# Revit family: Fallrohrstütze DN200-Set
name_source: partatom
category: HLS-Bauteile
revit_build: Autodesk Revit 2017 (Build: 20190507_1515(x64)
units: mm (PartAtom-declared; Revit-internal decimal feet)

## family parameters
Basisbauteil = Fläche
Beim Laden mit Abzugskörper schneiden = Nein
Bemaßung runder Anschluss = Durchmesser verwenden
Gemeinsam genutzt = Ja
Raumberechnungspunkt = Nein
Teiletyp = Normal

## types (1)
- Fallrohrstütze DN200
    6kt.Flanschmutter = Sechskantmutter : Sechskantmutter M12
    6kt.Schraube = 6kt.Schraube DIN EN ISO 4017 : M12x 30 SW19
    Abstandsmaß = 280 mm
    Abstandswinkeltyp = MEFA Winkel 2-Loch C-Profil 45
    Artikelnummer = 45020045
    B = 268 mm  [stored 0.879265 ft]
    Baustoffklasse = B2
    EAN = 4250928448415
    Fabrikat = MEFA
    Farbe Schalldämmeinlage = Schwarz
    Firma = MEFA Befestigungs- und Montagesysteme GmbH
    Gewicht = 4.08 kg
    Gewicht pro Bauteil = 4.08 kg
    Gewindeplattentyp = MEFA Zahnplatte S 36x20 M12
    Konsole = Konsole 45-45 : Konsole 45/45/2,  L=315mm
    Konsolentyp = C-Profil 45/45
    Kurztext1 = Fallrohrstützenbefestigung Set SML
    Kurztext2 = DN 200 / 210 mm Wandabstand 125 - 315 mm
    Langloch = 20 x 14 mm
    Lochabstand = 85 mm
    Länge Konsole = 315 mm  [stored 1.03346 ft]
    Material = Stahl
    Materialname C-Profil = S235JR
    Materialname Platte = S235JR
    Mengeneinheit = St
    Nennweite DN Rohr = 200 mm  [stored 0.656168 ft]
    Rohraußendurchmesser = 210 mm  [stored 0.688976 ft]
    Rohrschelle = MEFA RS Maxima PSM, AG M10-M12, Ø120-Ø275 mm, TPE : MEFA RS Maxima PSM, AG M10-M12, Ø207-Ø213 mm, TPE
    Rohrschellentyp = Maxima PSM
    Schalldämmeinlage = Gummi
    Setztiefe = M12x30
    Stärke Material Schalldämmeinlage = 6 mm
    Vorgabe-Ansicht = 1219 mm
    WA max. = 200 mm  [stored 0.656168 ft]
    max. Temperaturbeständigkeit = 100 °C
    max. Wandabstand = 315 mm
    max. zul. Last F1 = 1.49 kip
    max. zul. Last F2 = 0.75 kip
    min. Wandabstand = 125 mm
    vpe = 1 St

note: [stored X ft] marks values corroborated as IEEE doubles in the binary element streams (Revit-internal decimal feet)

## geometry (parser evidence)
native form markers: Sweep x5
no freeform markers — native parametric forms only
